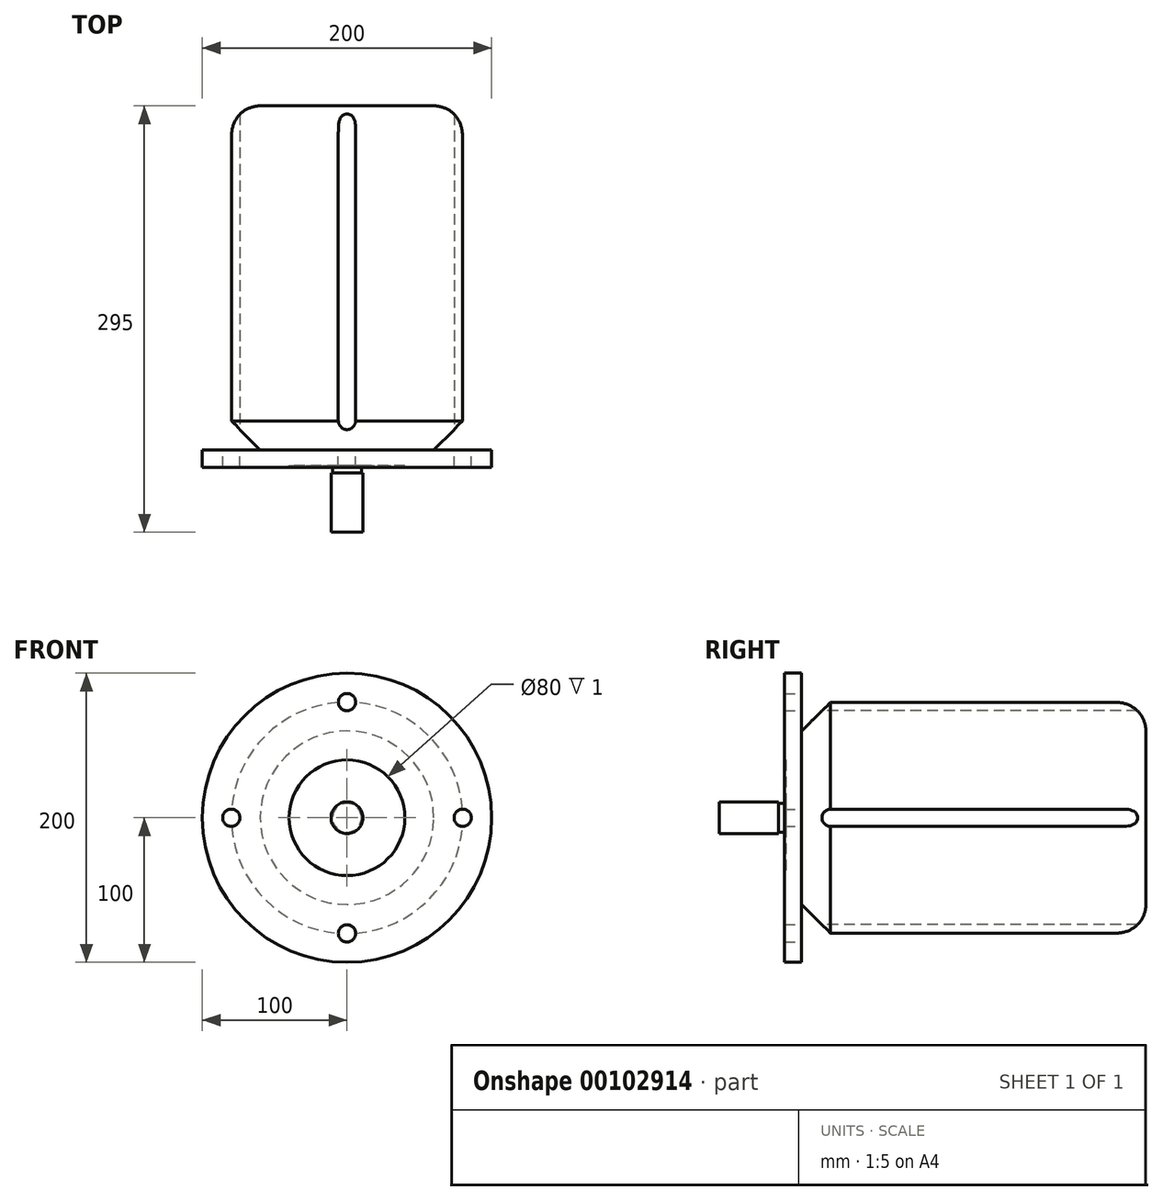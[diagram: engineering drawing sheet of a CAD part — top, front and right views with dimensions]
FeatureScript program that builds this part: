
annotation { "Feature Type Name" : "Feature", "Feature Type Description" : "" }
export const myFeature = defineFeature(function(context is Context, id is Id, definition is map)
    precondition{}
    {
        {
            var Q0;
            Q0=qCreatedBy(makeId("Right.planeOp"),FACE);
            var sketch = newSketch(context, id + "F0", { "sketchPlane" : qUnion([Q0])});
            skLineSegment(sketch, "E0", {"start": v(-45, 0) * mm, "end": v(-45, 11) * mm});
            skLineSegment(sketch, "E1", {"start": v(-45, 11) * mm, "end": v(-4, 11) * mm});
            skLineSegment(sketch, "E2", {"start": v(-4, 11) * mm, "end": v(-4, 10) * mm});
            skLineSegment(sketch, "E3", {"start": v(-4, 10) * mm, "end": v(1, 10) * mm});
            skLineSegment(sketch, "E4", {"start": v(0, 40) * mm, "end": v(0, 100) * mm});
            skLineSegment(sketch, "E5", {"start": v(0, 100) * mm, "end": v(12, 100) * mm});
            skLineSegment(sketch, "E6", {"start": v(12, 100) * mm, "end": v(12, 60) * mm});
            skLineSegment(sketch, "E7", {"start": v(12, 60) * mm, "end": v(32, 80) * mm});
            skLineSegment(sketch, "E8", {"start": v(32, 80) * mm, "end": v(230, 80) * mm});
            skLineSegment(sketch, "E9", {"start": v(-45, 0) * mm, "end": v(250, 0) * mm});
            skLineSegment(sketch, "E10", {"start": v(250, 0) * mm, "end": v(250, 60) * mm});
            skArc(sketch, "E11", {"start": v(250, 60) * mm, "mid": v(244.14, 74.14) * mm, "end": v(230, 80) * mm});
            skLineSegment(sketch, "E12", {"start": v(-45, 0) * mm, "end": v(-74.66, 0) * mm, "construction": true});
            skLineSegment(sketch, "E13", {"start": v(0, 40) * mm, "end": v(1, 40) * mm});
            skLineSegment(sketch, "E14", {"start": v(1, 40) * mm, "end": v(1, 10) * mm});
            skPoint(sketch, "E15.orphan", {"position": v(0, 10) * mm});
            skSolve(sketch);
        }
        {
            var Q0;
            Q0 = qSketchRegion(id + "F0", true);
            var Q1;
            Q1=sQuery(id+"F0.wireOp",EDGE,"E12");
            revolve(context, id + "F1", {"entities" : qUnion([Q0]), "axis" : qUnion([Q1]), "revolveType" : RevolveType.FULL});
        }
        {
            var Q0;
            Q0=makeQuery(id+"F1.opRevolve","SWEPT_FACE",FACE,{"disambiguationData":[OSD([sQuery(id+"F0.wireOp",EDGE,"E6")])]});
            var sketch = newSketch(context, id + "F2", { "sketchPlane" : qUnion([Q0])});
            skCircle(sketch, "E16", {"center": v(0, 80) * mm, "radius": 6 * mm});
            skCircle(sketch, "E17.1.0", {"center": v(80, 0) * mm, "radius": 6 * mm});
            skCircle(sketch, "E17.2.0", {"center": v(0, -80) * mm, "radius": 6 * mm});
            skCircle(sketch, "E17.3.0", {"center": v(-80, 0) * mm, "radius": 6 * mm});
            skPoint(sketch, "E17.center", {"position": v(0, 0) * mm});
            skLineSegment(sketch, "E17.anchor1", {"start": v(0, 0) * mm, "end": v(0, 80) * mm, "construction": true});
            skLineSegment(sketch, "E17.anchor2", {"start": v(0, 0) * mm, "end": v(-80, 0) * mm, "construction": true});
            skSolve(sketch);
        }
        {
            var Q0;
            Q0 = qSketchRegion(id + "F2", true);
            extrude(context, id + "F3", {"entities" : qUnion([Q0]), "operationType" : NewBodyOperationType.REMOVE, "oppositeDirection" : true, "depth" : 25 * mm});
        }
        {
            var Q0;
            Q0 = qSketchRegion(id + "F2", true);
            extrude(context, id + "F4", {"entities" : qUnion([Q0]), "operationType" : NewBodyOperationType.REMOVE, "endBound" : BoundingType.THROUGH_ALL, "depth" : 25 * mm});
        }
    });
